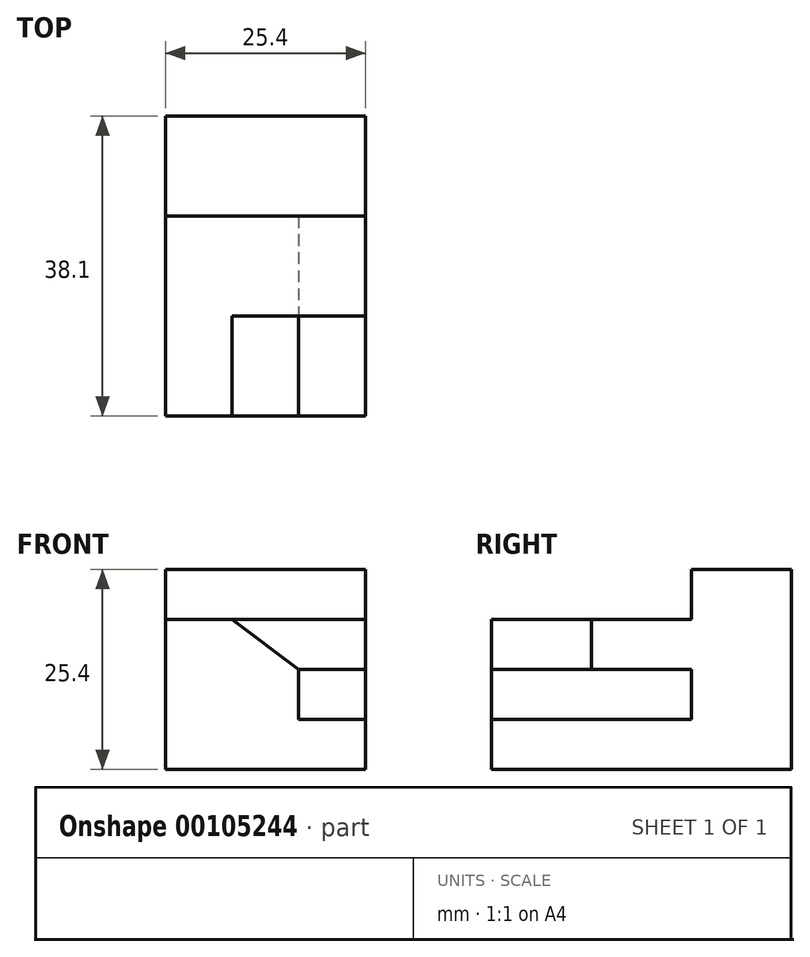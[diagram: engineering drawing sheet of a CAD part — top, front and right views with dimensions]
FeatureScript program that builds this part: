
annotation { "Feature Type Name" : "Feature", "Feature Type Description" : "" }
export const myFeature = defineFeature(function(context is Context, id is Id, definition is map)
    precondition{}
    {
        {
            var Q0;
            Q0=qCreatedBy(makeId("Front.planeOp"),FACE);
            var sketch = newSketch(context, id + "F0", { "sketchPlane" : qUnion([Q0])});
            skLineSegment(sketch, "E0", {"start": v(0, 0) * mm, "end": v(0, 6.35) * mm});
            skLineSegment(sketch, "E1", {"start": v(0, 6.35) * mm, "end": v(25.4, 6.35) * mm});
            skLineSegment(sketch, "E2", {"start": v(25.4, 6.35) * mm, "end": v(25.4, 0) * mm});
            skLineSegment(sketch, "E3", {"start": v(25.4, 0) * mm, "end": v(0, 0) * mm});
            skLineSegment(sketch, "E4", {"start": v(0, 6.35) * mm, "end": v(0, 19.05) * mm});
            skLineSegment(sketch, "E5", {"start": v(16.92, 6.35) * mm, "end": v(0, 6.35) * mm});
            skLineSegment(sketch, "E6", {"start": v(0, 19.05) * mm, "end": v(0, 25.37) * mm});
            skLineSegment(sketch, "E7", {"start": v(0, 25.37) * mm, "end": v(25.4, 6.35) * mm});
            skLineSegment(sketch, "E8", {"start": v(16.92, 6.35) * mm, "end": v(16.92, 12.7) * mm});
            skLineSegment(sketch, "E9", {"start": v(0, 19.05) * mm, "end": v(8.44, 19.05) * mm});
            skSolve(sketch);
        }
        {
            var Q0;
            Q0=qCreatedBy(makeId("Right.planeOp"),FACE);
            var sketch = newSketch(context, id + "F1", { "sketchPlane" : qUnion([Q0])});
            skLineSegment(sketch, "E10", {"start": v(0, 0) * mm, "end": v(38.1, 0) * mm});
            skLineSegment(sketch, "E11", {"start": v(38.1, 0) * mm, "end": v(38.1, 6.35) * mm});
            skLineSegment(sketch, "E12", {"start": v(38.1, 6.35) * mm, "end": v(0, 6.35) * mm});
            skLineSegment(sketch, "E13", {"start": v(0, 6.35) * mm, "end": v(0, 0) * mm});
            skLineSegment(sketch, "E14", {"start": v(12.7, 6.35) * mm, "end": v(12.7, 12.7) * mm});
            skLineSegment(sketch, "E15", {"start": v(12.7, 12.7) * mm, "end": v(25.4, 12.7) * mm});
            skLineSegment(sketch, "E16", {"start": v(25.4, 12.7) * mm, "end": v(25.4, 6.35) * mm});
            skLineSegment(sketch, "E17", {"start": v(25.4, 6.35) * mm, "end": v(12.7, 6.35) * mm});
            skLineSegment(sketch, "E18", {"start": v(12.7, 12.7) * mm, "end": v(12.7, 19.05) * mm});
            skLineSegment(sketch, "E19", {"start": v(12.7, 19.05) * mm, "end": v(25.4, 19.05) * mm});
            skLineSegment(sketch, "E20", {"start": v(25.4, 19.05) * mm, "end": v(25.4, 25.4) * mm});
            skLineSegment(sketch, "E21", {"start": v(25.4, 25.4) * mm, "end": v(38.1, 25.4) * mm});
            skLineSegment(sketch, "E22", {"start": v(38.1, 25.4) * mm, "end": v(38.1, 6.35) * mm});
            skLineSegment(sketch, "E23", {"start": v(25.4, 6.35) * mm, "end": v(25.4, 12.7) * mm});
            skSolve(sketch);
        }
        {
            var Q0;
            Q0=makeQuery(id+"F0.imprint","IMPRINT",FACE,{"disambiguationData":[TD([[makeQuery(id+"F0.imprint","IMPRINT",EDGE,{"derivedFrom":sQuery(id+"F0.wireOp",EDGE,"E0")}),-1.0]])]});
            var Q1;
            Q1=makeQuery(id+"F0.imprint","IMPRINT",FACE,{"disambiguationData":[TD([[makeQuery(id+"F0.imprint","IMPRINT",EDGE,{"derivedFrom":sQuery(id+"F0.wireOp",EDGE,"E4")}),-1.0]])]});
            extrude(context, id + "F2", {"entities" : qUnion([Q0, Q1]), "oppositeDirection" : true, "depth" : 25.4 * mm});
        }
        {
            var Q0;
            Q0=makeQuery(id+"F1.imprint","IMPRINT",FACE,{"disambiguationData":[TD([[makeQuery(id+"F1.imprint","IMPRINT",EDGE,{"derivedFrom":sQuery(id+"F1.wireOp",EDGE,"E10")}),1.0]])]});
            var Q1;
            Q1=makeQuery(id+"F1.imprint","IMPRINT",FACE,{"disambiguationData":[TD([[makeQuery(id+"F1.imprint","IMPRINT",EDGE,{"derivedFrom":sQuery(id+"F1.wireOp",EDGE,"E15")}),1.0]])]});
            extrude(context, id + "F3", {"entities" : qUnion([Q0, Q1]), "operationType" : NewBodyOperationType.ADD, "depth" : 25.4 * mm});
        }
    });
